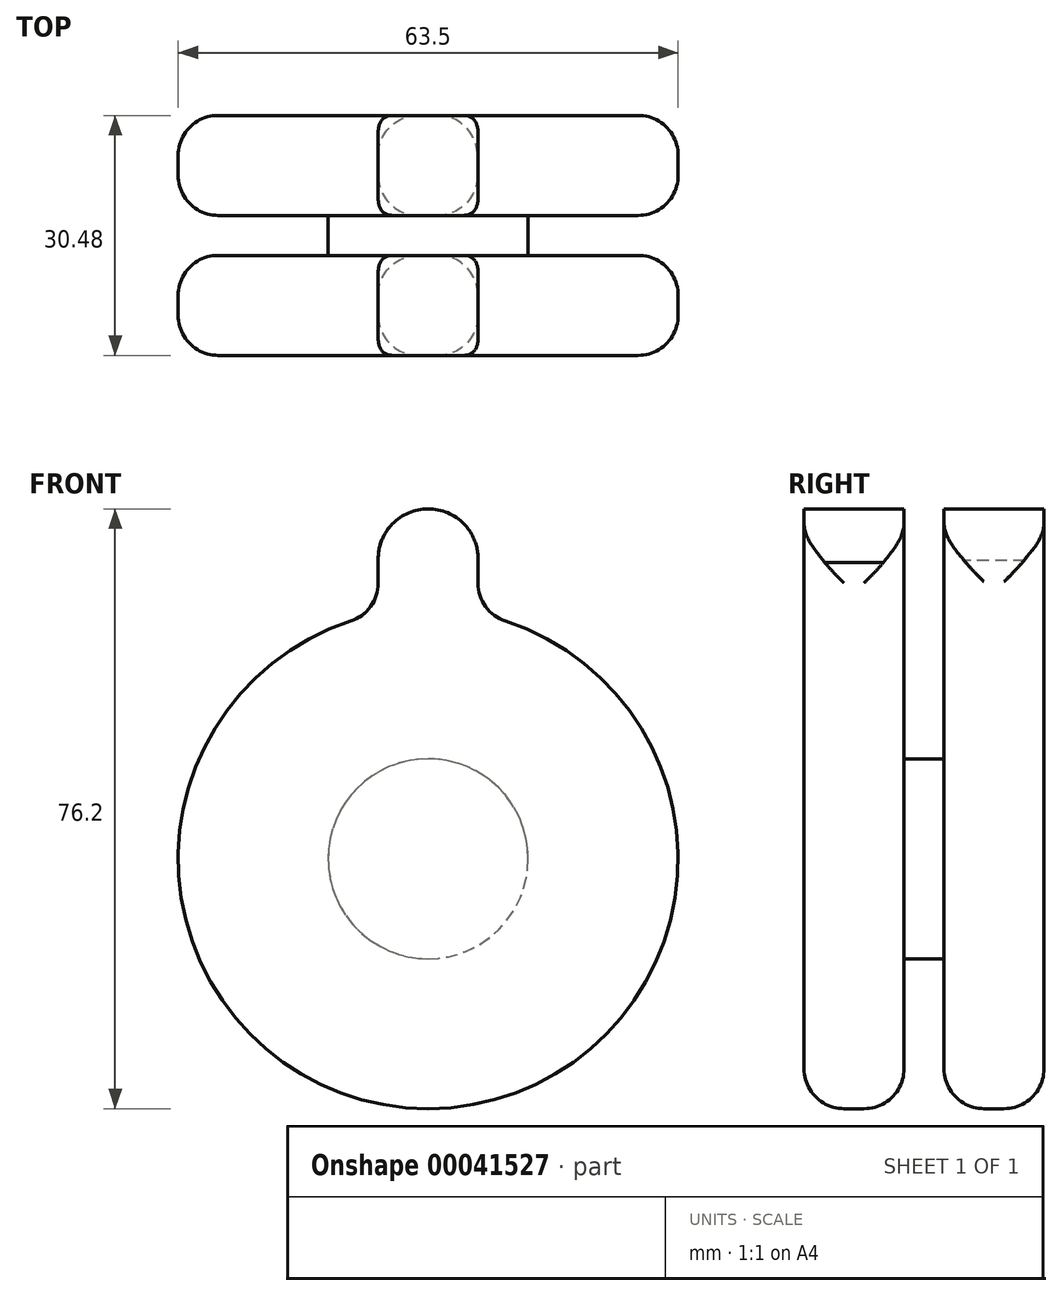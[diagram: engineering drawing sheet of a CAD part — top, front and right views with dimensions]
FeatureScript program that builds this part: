
annotation { "Feature Type Name" : "Feature", "Feature Type Description" : "" }
export const myFeature = defineFeature(function(context is Context, id is Id, definition is map)
    precondition{}
    {
        {
            var Q0;
            Q0=qCreatedBy(makeId("Front.planeOp"),FACE);
            var sketch = newSketch(context, id + "F0", { "sketchPlane" : qUnion([Q0])});
            skCircle(sketch, "E0", {"center": v(0, 0) * mm, "radius": 31.75 * mm});
            skCircle(sketch, "E1", {"center": v(0, 38.1) * mm, "radius": 6.35 * mm});
            skLineSegment(sketch, "E2", {"start": v(-6.34, 37.72) * mm, "end": v(-6.34, 31.11) * mm});
            skLineSegment(sketch, "E3", {"start": v(6.33, 31.11) * mm, "end": v(6.33, 37.64) * mm});
            skSolve(sketch);
        }
        {
            var Q0;
            Q0=qSketchRegion(id+"F0",true);
            extrude(context, id + "F1", {"entities" : qUnion([Q0]), "depth" : 12.7 * mm});
        }
        {
            var Q0;
            Q0=makeQuery(id+"F1.opExtrude","SWEPT_FACE",FACE,{"disambiguationData":[OSD([sQuery(id+"F0.wireOp",EDGE,"E0")])]});
            fillet(context, id + "F2", {"entities" : qUnion([Q0]), "radius" : 5.08 * mm, "tangentPropagation" : true, "allowEdgeOverflow" : false});
        }
        {
            var Q0;
            Q0=makeQuery(id+"F1.opExtrude","CAP_FACE",FACE,{"disambiguationData":[OSD([sQuery(id+"F0.wireOp",EDGE,"E0")])],"isStart":true});
            var sketch = newSketch(context, id + "F3", { "sketchPlane" : qUnion([Q0])});
            skCircle(sketch, "E4", {"center": v(0, 0) * mm, "radius": 12.7 * mm});
            skSolve(sketch);
        }
        {
            var Q0;
            Q0=qSketchRegion(id+"F3",true);
            extrude(context, id + "F4", {"entities" : qUnion([Q0]), "operationType" : NewBodyOperationType.ADD, "depth" : 5.08 * mm});
        }
        {
            var Q0;
            Q0=makeQuery(id+"F4.opExtrude","CAP_FACE",FACE,{"disambiguationData":[OSD([sQuery(id+"F3.wireOp",EDGE,"E4")])],"isStart":false});
            var sketch = newSketch(context, id + "F5", { "sketchPlane" : qUnion([Q0])});
            skCircle(sketch, "E5", {"center": v(0, 0) * mm, "radius": 31.75 * mm});
            skCircle(sketch, "E6", {"center": v(0, 38.1) * mm, "radius": 6.35 * mm});
            skLineSegment(sketch, "E7", {"start": v(-6.15, 31.15) * mm, "end": v(-6.35, 37.91) * mm});
            skLineSegment(sketch, "E8", {"start": v(6.35, 37.91) * mm, "end": v(6.35, 31.1) * mm});
            skSolve(sketch);
        }
        {
            var Q0;
            Q0=qSketchRegion(id+"F5",true);
            extrude(context, id + "F6", {"entities" : qUnion([Q0]), "operationType" : NewBodyOperationType.ADD, "depth" : 12.7 * mm});
        }
        {
            var Q0;
            Q0=makeQuery(id+"F6.opExtrude","SWEPT_FACE",FACE,{"disambiguationData":[OSD([sQuery(id+"F5.wireOp",EDGE,"E5")])]});
            fillet(context, id + "F7", {"entities" : qUnion([Q0]), "radius" : 5.08 * mm, "tangentPropagation" : true, "allowEdgeOverflow" : false});
        }
    });
